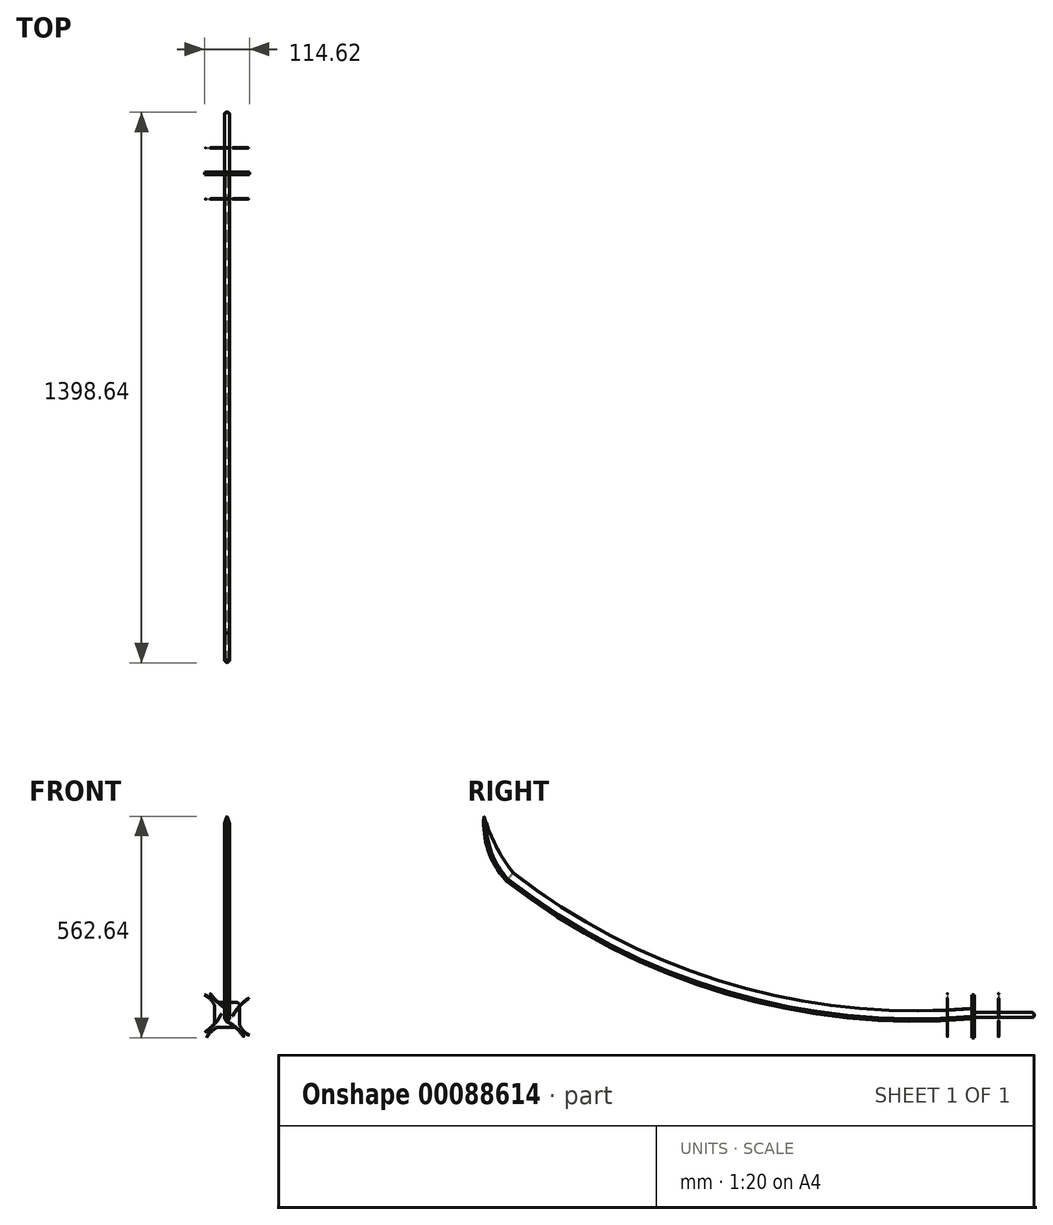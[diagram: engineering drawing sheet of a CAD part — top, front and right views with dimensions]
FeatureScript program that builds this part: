
annotation { "Feature Type Name" : "Feature", "Feature Type Description" : "" }
export const myFeature = defineFeature(function(context is Context, id is Id, definition is map)
    precondition{}
    {
        {
            var Q0;
            Q0=qCreatedBy(makeId("Right.planeOp"),FACE);
            var sketch = newSketch(context, id + "F0", { "sketchPlane" : qUnion([Q0])});
            skLineSegment(sketch, "E0.bottom", {"start": v(-21.77, 39.11) * mm, "end": v(-15.42, 39.11) * mm});
            skLineSegment(sketch, "E0.top", {"start": v(-21.77, -24.39) * mm, "end": v(-15.42, -24.39) * mm});
            skLineSegment(sketch, "E0.left", {"start": v(-21.77, 39.11) * mm, "end": v(-21.77, -24.39) * mm});
            skLineSegment(sketch, "E0.right", {"start": v(-15.42, 39.11) * mm, "end": v(-15.42, -24.39) * mm});
            skSolve(sketch);
        }
        {
            var Q0;
            Q0 = qSketchRegion(id + "F0", true);
            extrude(context, id + "F1", {"entities" : qUnion([Q0]), "depth" : 63.5 * mm});
        }
        {
            var Q0;
            Q0=makeQuery(id+"F1.opExtrude","SWEPT_FACE",FACE,{"disambiguationData":[OSD([sQuery(id+"F0.wireOp",EDGE,"E0.right")])]});
            var sketch = newSketch(context, id + "F2", { "sketchPlane" : qUnion([Q0])});
            skLineSegment(sketch, "E1.bottom", {"start": v(-38.1, 13.71) * mm, "end": v(-25.4, 13.71) * mm});
            skLineSegment(sketch, "E1.top", {"start": v(-38.1, 1.01) * mm, "end": v(-25.4, 1.01) * mm});
            skLineSegment(sketch, "E1.left", {"start": v(-38.1, 13.71) * mm, "end": v(-38.1, 1.01) * mm});
            skLineSegment(sketch, "E1.right", {"start": v(-25.4, 13.71) * mm, "end": v(-25.4, 1.01) * mm});
            skLineSegment(sketch, "E2", {"start": v(-63.5, 39.11) * mm, "end": v(0, 39.11) * mm});
            skLineSegment(sketch, "E3", {"start": v(-31.75, 13.71) * mm, "end": v(-31.75, 39.11) * mm});
            skPoint(sketch, "E3.startSnap0", {"position": v(-31.75, 39.11) * mm});
            skLineSegment(sketch, "E4", {"start": v(-63.5, 39.11) * mm, "end": v(-63.5, -24.39) * mm});
            skLineSegment(sketch, "E5", {"start": v(-63.5, -24.39) * mm, "end": v(0, -24.39) * mm});
            skLineSegment(sketch, "E6", {"start": v(0, -24.39) * mm, "end": v(0, 39.11) * mm});
            skLineSegment(sketch, "E7", {"start": v(-63.5, 7.36) * mm, "end": v(-38.1, 7.36) * mm});
            skLineSegment(sketch, "E8", {"start": v(-31.75, 1.01) * mm, "end": v(-31.75, -24.39) * mm});
            skLineSegment(sketch, "E9", {"start": v(-25.4, 7.36) * mm, "end": v(0, 7.36) * mm});
            skSolve(sketch);
        }
        {
            var Q0;
            {var subQ4=sQuery(id+"F2.wireOp",EDGE,"E1.left");var subQ6=sQuery(id+"F2.wireOp",EDGE,"E1.bottom");var subQ9=makeQuery(id+"F2.imprint","INTERSECT",VERTEX,{"derivedFrom":[subQ6,subQ4]});Q0=makeQuery(id+"F2.imprint","IMPRINT",FACE,{"disambiguationData":[TD([[makeQuery(id+"F2.imprint","IMPRINT",EDGE,{"disambiguationData":[TD([[subQ9,-1.0]])],"derivedFrom":subQ6}),-1.0]])]});}
            extrude(context, id + "F3", {"entities" : qUnion([Q0]), "operationType" : NewBodyOperationType.ADD, "depth" : 152.4 * mm});
        }
        {
            var Q0;
            Q0=makeQuery(id+"F3.opExtrude","SWEPT_EDGE",EDGE,{"disambiguationData":[OSD([sQuery(id+"F2.wireOp",EDGE,"E1.bottom"),sQuery(id+"F2.wireOp",EDGE,"E1.right")])]});
            var Q1;
            Q1=makeQuery(id+"F3.opExtrude","SWEPT_EDGE",EDGE,{"disambiguationData":[OSD([sQuery(id+"F2.wireOp",EDGE,"E1.top"),sQuery(id+"F2.wireOp",EDGE,"E1.right")])]});
            var Q2;
            Q2=makeQuery(id+"F3.opExtrude","SWEPT_EDGE",EDGE,{"disambiguationData":[OSD([sQuery(id+"F2.wireOp",EDGE,"E1.top"),sQuery(id+"F2.wireOp",EDGE,"E1.left")])]});
            var Q3;
            Q3=makeQuery(id+"F3.opExtrude","SWEPT_EDGE",EDGE,{"disambiguationData":[OSD([sQuery(id+"F2.wireOp",EDGE,"E1.bottom"),sQuery(id+"F2.wireOp",EDGE,"E1.left")])]});
            fillet(context, id + "F4", {"entities" : qUnion([Q0, Q1, Q2, Q3]), "radius" : 3.05 * mm, "tangentPropagation" : true, "allowEdgeOverflow" : false});
        }
        {
            var Q0;
            Q0=makeQuery(id+"F3.opExtrude","CAP_FACE",FACE,{"disambiguationData":[OSD([sQuery(id+"F2.wireOp",EDGE,"E1.bottom"),sQuery(id+"F2.wireOp",EDGE,"E1.top"),sQuery(id+"F2.wireOp",EDGE,"E1.left"),sQuery(id+"F2.wireOp",EDGE,"E1.right")])],"isStart":false});
            fillet(context, id + "F5", {"entities" : qUnion([Q0]), "radius" : 5.08 * mm, "tangentPropagation" : true, "allowEdgeOverflow" : false});
        }
        {
            var Q0;
            Q0=makeQuery(id+"F1.opExtrude","SWEPT_FACE",FACE,{"disambiguationData":[OSD([sQuery(id+"F0.wireOp",EDGE,"E0.left")])]});
            var sketch = newSketch(context, id + "F6", { "sketchPlane" : qUnion([Q0])});
            skArc(sketch, "E10", {"start": v(0, -15.84) * mm, "mid": v(-11.86, -31.73) * mm, "end": v(-19.67, -49.95) * mm});
            skArc(sketch, "E11", {"start": v(6.17, -24.39) * mm, "mid": v(-8.7, -35.2) * mm, "end": v(-19.67, -49.95) * mm});
            skLineSegment(sketch, "E12", {"start": v(31.75, 39.11) * mm, "end": v(31.75, -24.39) * mm});
            skCircle(sketch, "E13", {"center": v(31.75, 7.36) * mm, "radius": 14.7 * mm});
            skSolve(sketch);
        }
        {
            var Q0;
            {var subQ0=sQuery(id+"F6.wireOp",EDGE,"E10");Q0=makeQuery(id+"F6.imprint","IMPRINT",FACE,{"disambiguationData":[TD([[makeQuery(id+"F6.imprint","IMPRINT",EDGE,{"derivedFrom":subQ0}),1.0]])]});}
            extrude(context, id + "F7", {"entities" : qUnion([Q0]), "oppositeDirection" : true, "depth" : 6.35 * mm});
        }
        {
            var Q0;
            Q0=makeQuery(id+"F7.opExtrude","SWEPT_BODY",BODY,{"disambiguationData":[OSD([sQuery(id+"F0.wireOp",EDGE,"E0.top"),sQuery(id+"F0.wireOp",EDGE,"E0.left"),sQuery(id+"F6.wireOp",EDGE,"E10"),sQuery(id+"F6.wireOp",EDGE,"E11")])]});
            var Q1;
            Q1=sQuery(id+"F6.wireOp",EDGE,"E13");
            circularPattern(context, id + "F8", {"operationType" : NewBodyOperationType.ADD, "entities" : qUnion([Q0]), "axis" : qUnion([Q1]), "angle" : 90 * degree, "instanceCount" : 4});
        }
        {
            var Q0;
            Q0=makeQuery(id+"F8.opPattern","COPY",EDGE,{"derivedFrom":makeQuery(id+"F7.opExtrude","SWEPT_EDGE",EDGE,{"disambiguationData":[OSD([sQuery(id+"F6.wireOp",EDGE,"E10"),sQuery(id+"F6.wireOp",EDGE,"E11")])]}),"instanceName":"2"});
            chamfer(context, id + "F9", {"entities" : qUnion([Q0]), "width" : 5.08 * mm, "tangentPropagation" : true});
        }
        {
            var Q0;
            Q0=makeQuery(id+"F9.opChamfer","BLEND_FACE",FACE,{"disambiguationData":[OSD([sQuery(id+"F6.wireOp",EDGE,"E10"),sQuery(id+"F6.wireOp",EDGE,"E11")])]});
            var sketch = newSketch(context, id + "F10", { "sketchPlane" : qUnion([Q0])});
            skCircle(sketch, "E14", {"center": v(46.39, -15.42) * mm, "radius": 0.5 * mm});
            skSolve(sketch);
        }
        {
            var Q0;
            {var subQ0=makeQuery(id+"F7.opExtrude","CAP_FACE",FACE,{"disambiguationData":[OSD([sQuery(id+"F0.wireOp",EDGE,"E0.top"),sQuery(id+"F0.wireOp",EDGE,"E0.left"),sQuery(id+"F6.wireOp",EDGE,"E10"),sQuery(id+"F6.wireOp",EDGE,"E11")])],"isStart":false});Q0=makeQuery(id+"F8.boolean.opBoolean","MERGE",FACE,{"derivedFrom":[makeQuery(id+"F1.opExtrude","SWEPT_FACE",FACE,{"disambiguationData":[OSD([sQuery(id+"F0.wireOp",EDGE,"E0.right")])]}),subQ0,makeQuery(id+"F8.opPattern","COPY",FACE,{"derivedFrom":subQ0,"instanceName":"1"}),makeQuery(id+"F8.opPattern","COPY",FACE,{"derivedFrom":subQ0,"instanceName":"2"}),makeQuery(id+"F8.opPattern","COPY",FACE,{"derivedFrom":subQ0,"instanceName":"3"})]});}
            var sketch = newSketch(context, id + "F11", { "sketchPlane" : qUnion([Q0])});
            skArc(sketch, "E15", {"start": v(-37.2, 12.82) * mm, "mid": v(-56.26, 39.29) * mm, "end": v(-81.2, 60.3) * mm});
            skSolve(sketch);
        }
        {
            var Q0;
            {var subQ0=sQuery(id+"F10.wireOp",EDGE,"E14");var subQ1=sQuery(id+"F6.wireOp",EDGE,"E11");var subQ2=sQuery(id+"F6.wireOp",EDGE,"E10");var subQ3=makeQuery(id+"F7.opExtrude","CAP_FACE",FACE,{"disambiguationData":[OSD([sQuery(id+"F0.wireOp",EDGE,"E0.top"),sQuery(id+"F0.wireOp",EDGE,"E0.left"),subQ2,subQ1])],"isStart":false});var subQ4=makeQuery(id+"F9.opChamfer","BLEND_EDGE",EDGE,{"blendedFrom":[makeQuery(id+"F8.opPattern","COPY",EDGE,{"derivedFrom":makeQuery(id+"F7.opExtrude","SWEPT_EDGE",EDGE,{"disambiguationData":[OSD([subQ2,subQ1])]}),"instanceName":"2"}),makeQuery(id+"F8.boolean.opBoolean","MERGE",FACE,{"derivedFrom":[makeQuery(id+"F1.opExtrude","SWEPT_FACE",FACE,{"disambiguationData":[OSD([sQuery(id+"F0.wireOp",EDGE,"E0.right")])]}),subQ3,makeQuery(id+"F8.opPattern","COPY",FACE,{"derivedFrom":subQ3,"instanceName":"1"}),makeQuery(id+"F8.opPattern","COPY",FACE,{"derivedFrom":subQ3,"instanceName":"2"}),makeQuery(id+"F8.opPattern","COPY",FACE,{"derivedFrom":subQ3,"instanceName":"3"})]})],"blendedInto":[makeQuery(id+"F8.boolean.opBoolean","MERGE",FACE,{"derivedFrom":[makeQuery(id+"F1.opExtrude","SWEPT_FACE",FACE,{"disambiguationData":[OSD([sQuery(id+"F0.wireOp",EDGE,"E0.right")])]}),subQ3,makeQuery(id+"F8.opPattern","COPY",FACE,{"derivedFrom":subQ3,"instanceName":"1"}),makeQuery(id+"F8.opPattern","COPY",FACE,{"derivedFrom":subQ3,"instanceName":"2"}),makeQuery(id+"F8.opPattern","COPY",FACE,{"derivedFrom":subQ3,"instanceName":"3"})]})]});var subQ5=makeQuery(id+"F10.imprint","INTERSECT",VERTEX,{"disambiguationData":[OD(0.0)],"derivedFrom":[subQ4,subQ0]});Q0=makeQuery(id+"F10.imprint","IMPRINT",FACE,{"disambiguationData":[TD([[makeQuery(id+"F10.imprint","IMPRINT",EDGE,{"disambiguationData":[TD([[subQ5,-1.0]])],"derivedFrom":subQ0}),1.0]])]});}
            var Q1;
            Q1=sQuery(id+"F11.wireOp",EDGE,"E15");
            sweep(context, id + "F12", {"profiles" : qUnion([Q0]), "path" : qUnion([Q1])});
        }
        {
            var Q0;
            Q0=makeQuery(id+"F12.opSweep","SWEPT_BODY",BODY,{"disambiguationData":[OSD([sQuery(id+"F0.wireOp",EDGE,"E0.top"),sQuery(id+"F0.wireOp",EDGE,"E0.left"),sQuery(id+"F0.wireOp",EDGE,"E0.right"),sQuery(id+"F6.wireOp",EDGE,"E10"),sQuery(id+"F6.wireOp",EDGE,"E11"),sQuery(id+"F10.wireOp",EDGE,"E14"),sQuery(id+"F11.wireOp",EDGE,"E15")])]});
            var Q1;
            Q1=sQuery(id+"F6.wireOp",EDGE,"E13");
            circularPattern(context, id + "F13", {"entities" : qUnion([Q0]), "axis" : qUnion([Q1]), "angle" : 90 * degree, "instanceCount" : 4});
        }
        {
            var Q0;
            {var subQ0=sQuery(id+"F0.wireOp",EDGE,"E0.left");var subQ1=makeQuery(id+"F7.opExtrude","CAP_FACE",FACE,{"disambiguationData":[OSD([sQuery(id+"F0.wireOp",EDGE,"E0.top"),subQ0,sQuery(id+"F6.wireOp",EDGE,"E10"),sQuery(id+"F6.wireOp",EDGE,"E11")])],"isStart":true});Q0=makeQuery(id+"F8.boolean.opBoolean","MERGE",FACE,{"derivedFrom":[makeQuery(id+"F1.opExtrude","SWEPT_FACE",FACE,{"disambiguationData":[OSD([subQ0])]}),subQ1,makeQuery(id+"F8.opPattern","COPY",FACE,{"derivedFrom":subQ1,"instanceName":"1"}),makeQuery(id+"F8.opPattern","COPY",FACE,{"derivedFrom":subQ1,"instanceName":"2"}),makeQuery(id+"F8.opPattern","COPY",FACE,{"derivedFrom":subQ1,"instanceName":"3"})]});}
            cPlane(context, id + "F14", {"entities" : qUnion([Q0]), "cplaneType" : CPlaneType.OFFSET, "offset" : 3.17 * mm, "oppositeDirection" : true, "width" : 152.4 * mm, "height" : 152.4 * mm});
        }
        {
            var Q0;
            Q0=makeQuery(id+"F12.opSweep","SWEPT_BODY",BODY,{"disambiguationData":[OSD([sQuery(id+"F0.wireOp",EDGE,"E0.top"),sQuery(id+"F0.wireOp",EDGE,"E0.left"),sQuery(id+"F0.wireOp",EDGE,"E0.right"),sQuery(id+"F6.wireOp",EDGE,"E10"),sQuery(id+"F6.wireOp",EDGE,"E11"),sQuery(id+"F10.wireOp",EDGE,"E14"),sQuery(id+"F11.wireOp",EDGE,"E15")])]});
            var Q1;
            Q1=makeQuery(id+"F13.opPattern","COPY",BODY,{"derivedFrom":makeQuery(id+"F12.opSweep","SWEPT_BODY",BODY,{"disambiguationData":[OSD([sQuery(id+"F0.wireOp",EDGE,"E0.top"),sQuery(id+"F0.wireOp",EDGE,"E0.left"),sQuery(id+"F0.wireOp",EDGE,"E0.right"),sQuery(id+"F6.wireOp",EDGE,"E10"),sQuery(id+"F6.wireOp",EDGE,"E11"),sQuery(id+"F10.wireOp",EDGE,"E14"),sQuery(id+"F11.wireOp",EDGE,"E15")])]}),"instanceName":"1"});
            var Q2;
            Q2=makeQuery(id+"F13.opPattern","COPY",BODY,{"derivedFrom":makeQuery(id+"F12.opSweep","SWEPT_BODY",BODY,{"disambiguationData":[OSD([sQuery(id+"F0.wireOp",EDGE,"E0.top"),sQuery(id+"F0.wireOp",EDGE,"E0.left"),sQuery(id+"F0.wireOp",EDGE,"E0.right"),sQuery(id+"F6.wireOp",EDGE,"E10"),sQuery(id+"F6.wireOp",EDGE,"E11"),sQuery(id+"F10.wireOp",EDGE,"E14"),sQuery(id+"F11.wireOp",EDGE,"E15")])]}),"instanceName":"2"});
            var Q3;
            Q3=makeQuery(id+"F13.opPattern","COPY",BODY,{"derivedFrom":makeQuery(id+"F12.opSweep","SWEPT_BODY",BODY,{"disambiguationData":[OSD([sQuery(id+"F0.wireOp",EDGE,"E0.top"),sQuery(id+"F0.wireOp",EDGE,"E0.left"),sQuery(id+"F0.wireOp",EDGE,"E0.right"),sQuery(id+"F6.wireOp",EDGE,"E10"),sQuery(id+"F6.wireOp",EDGE,"E11"),sQuery(id+"F10.wireOp",EDGE,"E14"),sQuery(id+"F11.wireOp",EDGE,"E15")])]}),"instanceName":"3"});
            var Q4;
            Q4=qCreatedBy(id+"F14.planeOp",FACE);
            mirror(context, id + "F15", {"entities" : qUnion([Q0, Q1, Q2, Q3]), "mirrorPlane" : qUnion([Q4])});
        }
        {
            var Q0;
            {var subQ0=sQuery(id+"F0.wireOp",EDGE,"E0.left");var subQ1=makeQuery(id+"F7.opExtrude","CAP_FACE",FACE,{"disambiguationData":[OSD([sQuery(id+"F0.wireOp",EDGE,"E0.top"),subQ0,sQuery(id+"F6.wireOp",EDGE,"E10"),sQuery(id+"F6.wireOp",EDGE,"E11")])],"isStart":true});Q0=makeQuery(id+"F8.boolean.opBoolean","MERGE",FACE,{"derivedFrom":[makeQuery(id+"F1.opExtrude","SWEPT_FACE",FACE,{"disambiguationData":[OSD([subQ0])]}),subQ1,makeQuery(id+"F8.opPattern","COPY",FACE,{"derivedFrom":subQ1,"instanceName":"1"}),makeQuery(id+"F8.opPattern","COPY",FACE,{"derivedFrom":subQ1,"instanceName":"2"}),makeQuery(id+"F8.opPattern","COPY",FACE,{"derivedFrom":subQ1,"instanceName":"3"})]});}
            var sketch = newSketch(context, id + "F16", { "sketchPlane" : qUnion([Q0])});
            skLineSegment(sketch, "E16.bottom", {"start": v(25.8, 24.15) * mm, "end": v(38.04, 24.15) * mm});
            skLineSegment(sketch, "E16.top", {"start": v(25.8, -4.02) * mm, "end": v(38.04, -4.02) * mm});
            skLineSegment(sketch, "E16.left", {"start": v(25.8, 24.15) * mm, "end": v(25.8, -4.02) * mm});
            skLineSegment(sketch, "E16.right", {"start": v(38.04, 24.15) * mm, "end": v(38.04, -4.02) * mm});
            skSolve(sketch);
        }
        {
            var Q0;
            Q0=makeQuery(id+"F1.opExtrude","CAP_FACE",FACE,{"disambiguationData":[OSD([sQuery(id+"F0.wireOp",EDGE,"E0.bottom"),sQuery(id+"F0.wireOp",EDGE,"E0.top"),sQuery(id+"F0.wireOp",EDGE,"E0.left"),sQuery(id+"F0.wireOp",EDGE,"E0.right")])],"isStart":false});
            cPlane(context, id + "F17", {"entities" : qUnion([Q0]), "cplaneType" : CPlaneType.OFFSET, "offset" : 31.75 * mm, "oppositeDirection" : true, "width" : 152.4 * mm, "height" : 152.4 * mm});
        }
        {
            var Q0;
            Q0=qCreatedBy(id+"F17.planeOp",FACE);
            var sketch = newSketch(context, id + "F18", { "sketchPlane" : qUnion([Q0])});
            skArc(sketch, "E17", {"start": v(-1199.07, 355.26) * mm, "mid": v(-643.46, 69.48) * mm, "end": v(-21.9, 5.99) * mm});
            skSolve(sketch);
        }
        {
            var Q0;
            Q0=makeQuery(id+"F16.imprint","IMPRINT",FACE,{"disambiguationData":[TD([[makeQuery(id+"F16.imprint","IMPRINT",EDGE,{"derivedFrom":sQuery(id+"F16.wireOp",EDGE,"E16.bottom")}),-1.0]])]});
            var Q1;
            Q1=sQuery(id+"F18.wireOp",EDGE,"E17");
            sweep(context, id + "F19", {"profiles" : qUnion([Q0]), "path" : qUnion([Q1])});
        }
        {
            var Q0;
            Q0=makeQuery(id+"F19.opSweep","SWEPT_FACE",FACE,{"disambiguationData":[OSD([sQuery(id+"F16.wireOp",EDGE,"E16.right"),sQuery(id+"F18.wireOp",EDGE,"E17")])]});
            var sketch = newSketch(context, id + "F20", { "sketchPlane" : qUnion([Q0])});
            skArc(sketch, "E18", {"start": v(-1261.82, 516.05) * mm, "mid": v(-1251.86, 425.92) * mm, "end": v(-1205.77, 347.83) * mm});
            skArc(sketch, "E19", {"start": v(-1261.82, 516.05) * mm, "mid": v(-1231.5, 438.57) * mm, "end": v(-1186.64, 368.5) * mm});
            skSolve(sketch);
        }
        {
            var Q0;
            Q0 = qSketchRegion(id + "F20", true);
            var Q1;
            Q1=makeQuery(id+"F20.imprint","IMPRINT",FACE,{"disambiguationData":[TD([[makeQuery(id+"F20.imprint","IMPRINT",EDGE,{"derivedFrom":sQuery(id+"F20.wireOp",EDGE,"Nidjj9JY-Hp3C-K2F9-S2e9-VJieEoEKwBsS")}),-1.0]])]});
            var Q2;
            Q2=makeQuery(id+"F20.imprint","IMPRINT",FACE,{"disambiguationData":[TD([[makeQuery(id+"F20.imprint","IMPRINT",EDGE,{"derivedFrom":sQuery(id+"F20.wireOp",EDGE,"E18")}),1.0]])]});
            extrude(context, id + "F21", {"entities" : qUnion([Q0, Q1, Q2]), "operationType" : NewBodyOperationType.ADD, "oppositeDirection" : true, "depth" : 12.7 * mm});
        }
        {
            var Q0;
            Q0=makeQuery(id+"F19.opSweep","SWEPT_EDGE",EDGE,{"disambiguationData":[OSD([sQuery(id+"F16.wireOp",EDGE,"E16.top"),sQuery(id+"F16.wireOp",EDGE,"E16.left"),sQuery(id+"F18.wireOp",EDGE,"E17")])]});
            var Q1;
            Q1=makeQuery(id+"F19.opSweep","SWEPT_EDGE",EDGE,{"disambiguationData":[OSD([sQuery(id+"F16.wireOp",EDGE,"E16.top"),sQuery(id+"F16.wireOp",EDGE,"E16.right"),sQuery(id+"F18.wireOp",EDGE,"E17")])]});
            chamfer(context, id + "F22", {"entities" : qUnion([Q0, Q1]), "width" : 7.62 * mm, "tangentPropagation" : true});
        }
        {
            var Q0;
            Q0=makeQuery(id+"F21.opExtrude","CAP_EDGE",EDGE,{"disambiguationData":[OSD([sQuery(id+"F20.wireOp",EDGE,"E18")])],"isStart":false});
            var Q1;
            Q1=makeQuery(id+"F21.opExtrude","CAP_EDGE",EDGE,{"disambiguationData":[OSD([sQuery(id+"F20.wireOp",EDGE,"E18")])],"isStart":true});
            chamfer(context, id + "F23", {"entities" : qUnion([Q0, Q1]), "width" : 7.62 * mm, "tangentPropagation" : true});
        }
        {
            var Q0;
            Q0=makeQuery(id+"F19.opSweep","SWEPT_FACE",FACE,{"disambiguationData":[OSD([sQuery(id+"F16.wireOp",EDGE,"E16.left"),sQuery(id+"F18.wireOp",EDGE,"E17")])]});
            extrude(context, id + "F24", {"entities" : qUnion([Q0]), "depth" : 0.01 * mm});
        }
        {
            var Q0;
            Q0=makeQuery(id+"F21.opExtrude","CAP_FACE",FACE,{"disambiguationData":[OSD([sQuery(id+"F16.wireOp",EDGE,"E16.right"),sQuery(id+"F18.wireOp",VERTEX,"E17.start"),sQuery(id+"F20.wireOp",EDGE,"E18"),sQuery(id+"F20.wireOp",EDGE,"E19")])],"isStart":false});
            extrude(context, id + "F25", {"entities" : qUnion([Q0]), "operationType" : NewBodyOperationType.ADD, "depth" : 0.01 * mm});
        }
        {
            var Q0;
            {var subQ0=sQuery(id+"F16.wireOp",EDGE,"E16.right");Q0=makeQuery(id+"F21.boolean.opBoolean","MERGE",FACE,{"derivedFrom":[makeQuery(id+"F19.opSweep","SWEPT_FACE",FACE,{"disambiguationData":[OSD([subQ0,sQuery(id+"F18.wireOp",EDGE,"E17")])]}),makeQuery(id+"F21.opExtrude","CAP_FACE",FACE,{"disambiguationData":[OSD([subQ0,sQuery(id+"F18.wireOp",VERTEX,"E17.start"),sQuery(id+"F20.wireOp",EDGE,"E18"),sQuery(id+"F20.wireOp",EDGE,"E19")])],"isStart":true})]});}
            extrude(context, id + "F26", {"entities" : qUnion([Q0]), "depth" : 0.01 * mm});
        }
        {
            var Q0;
            {var subQ0=sQuery(id+"F0.wireOp",EDGE,"E0.left");var subQ1=makeQuery(id+"F7.opExtrude","CAP_FACE",FACE,{"disambiguationData":[OSD([sQuery(id+"F0.wireOp",EDGE,"E0.top"),subQ0,sQuery(id+"F6.wireOp",EDGE,"E10"),sQuery(id+"F6.wireOp",EDGE,"E11")])],"isStart":true});Q0=makeQuery(id+"F8.boolean.opBoolean","MERGE",FACE,{"derivedFrom":[makeQuery(id+"F1.opExtrude","SWEPT_FACE",FACE,{"disambiguationData":[OSD([subQ0])]}),subQ1,makeQuery(id+"F8.opPattern","COPY",FACE,{"derivedFrom":subQ1,"instanceName":"1"}),makeQuery(id+"F8.opPattern","COPY",FACE,{"derivedFrom":subQ1,"instanceName":"2"}),makeQuery(id+"F8.opPattern","COPY",FACE,{"derivedFrom":subQ1,"instanceName":"3"})]});}
            var sketch = newSketch(context, id + "F27", { "sketchPlane" : qUnion([Q0])});
            skLineSegment(sketch, "E20.bottom", {"start": v(25.8, 24.38) * mm, "end": v(38.01, 24.38) * mm});
            skLineSegment(sketch, "E20.top", {"start": v(25.8, 22.6) * mm, "end": v(38.01, 22.6) * mm});
            skLineSegment(sketch, "E20.left", {"start": v(25.8, 24.38) * mm, "end": v(25.8, 22.6) * mm});
            skLineSegment(sketch, "E20.right", {"start": v(38.01, 24.38) * mm, "end": v(38.01, 22.6) * mm});
            skSolve(sketch);
        }
        {
            var Q0;
            Q0=makeQuery(id+"F27.imprint","IMPRINT",FACE,{"disambiguationData":[TD([[makeQuery(id+"F27.imprint","IMPRINT",EDGE,{"derivedFrom":sQuery(id+"F27.wireOp",EDGE,"E20.bottom")}),-1.0]])]});
            var Q1;
            Q1=makeQuery(id+"F19.opSweep","SWEPT_EDGE",EDGE,{"disambiguationData":[OSD([sQuery(id+"F16.wireOp",EDGE,"E16.bottom"),sQuery(id+"F16.wireOp",EDGE,"E16.left"),sQuery(id+"F18.wireOp",EDGE,"E17")])]});
            sweep(context, id + "F28", {"profiles" : qUnion([Q0]), "path" : qUnion([Q1])});
        }
        {
            var Q0;
            Q0=makeQuery(id+"F28.opSweep","CAP_FACE",FACE,{"disambiguationData":[OSD([sQuery(id+"F16.wireOp",EDGE,"E16.bottom"),sQuery(id+"F16.wireOp",EDGE,"E16.left"),sQuery(id+"F18.wireOp",EDGE,"E17"),sQuery(id+"F27.wireOp",EDGE,"E20.bottom"),sQuery(id+"F27.wireOp",EDGE,"E20.top"),sQuery(id+"F27.wireOp",EDGE,"E20.left"),sQuery(id+"F27.wireOp",EDGE,"E20.right")])],"isStart":false});
            var Q1;
            Q1=makeQuery(id+"F26.opExtrude","CAP_EDGE",EDGE,{"disambiguationData":[OSD([sQuery(id+"F20.wireOp",EDGE,"E19")])],"isStart":false});
            sweep(context, id + "F29", {"profiles" : qUnion([Q0]), "path" : qUnion([Q1])});
        }
        {
            var Q0;
            Q0=makeQuery(id+"F29.opSweep","SWEPT_FACE",FACE,{"disambiguationData":[OSD([sQuery(id+"F16.wireOp",EDGE,"E16.bottom"),sQuery(id+"F16.wireOp",EDGE,"E16.left"),sQuery(id+"F18.wireOp",EDGE,"E17"),sQuery(id+"F20.wireOp",EDGE,"E19"),sQuery(id+"F27.wireOp",EDGE,"E20.left")])]});
            extrude(context, id + "F30", {"entities" : qUnion([Q0]), "operationType" : NewBodyOperationType.ADD, "depth" : 0.44 * mm});
        }
    });
